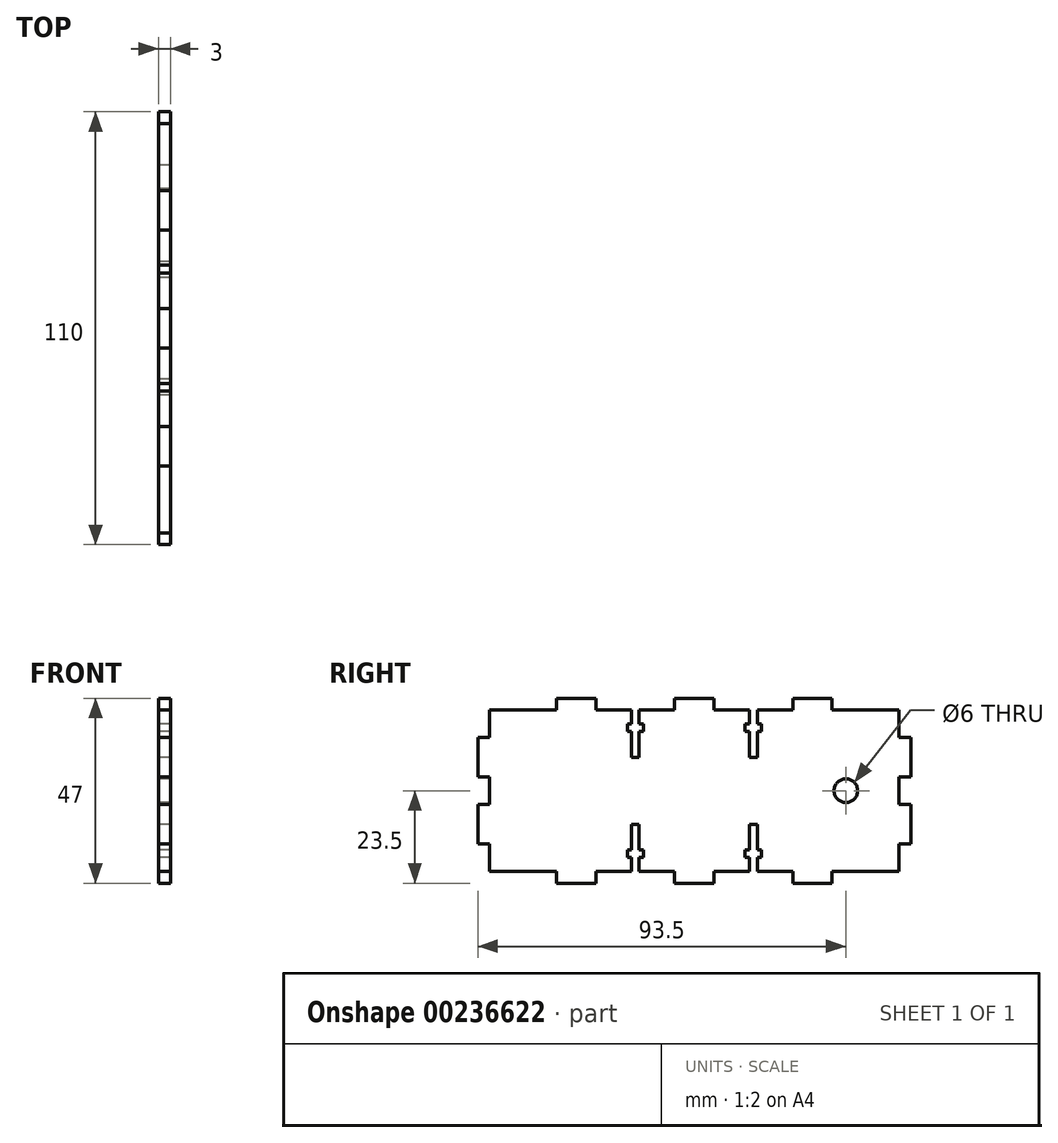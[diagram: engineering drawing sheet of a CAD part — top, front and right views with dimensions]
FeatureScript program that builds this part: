
annotation { "Feature Type Name" : "Feature", "Feature Type Description" : "" }
export const myFeature = defineFeature(function(context is Context, id is Id, definition is map)
    precondition{}
    {
        {
            var Q0;
            Q0=qCreatedBy(makeId("Right.planeOp"),FACE);
            var sketch = newSketch(context, id + "F0", { "sketchPlane" : qUnion([Q0])});
            skLineSegment(sketch, "E0", {"start": v(0, 0) * mm, "end": v(0, 7) * mm});
            skLineSegment(sketch, "E1", {"start": v(0, 7) * mm, "end": v(-3, 7) * mm});
            skLineSegment(sketch, "E2", {"start": v(-3, 7) * mm, "end": v(-3, 17) * mm});
            skLineSegment(sketch, "E3", {"start": v(-3, 17) * mm, "end": v(0, 17) * mm});
            skLineSegment(sketch, "E4", {"start": v(0, 17) * mm, "end": v(0, 20.5) * mm});
            skLineSegment(sketch, "E5", {"start": v(0, 0) * mm, "end": v(17, 0) * mm});
            skLineSegment(sketch, "E6", {"start": v(17, 0) * mm, "end": v(17, -3) * mm});
            skLineSegment(sketch, "E7", {"start": v(17, -3) * mm, "end": v(27, -3) * mm});
            skLineSegment(sketch, "E8", {"start": v(27, 0) * mm, "end": v(27, -3) * mm});
            skLineSegment(sketch, "E9", {"start": v(27, 0) * mm, "end": v(36, 0) * mm});
            skLineSegment(sketch, "E10", {"start": v(36, 0) * mm, "end": v(36, 3.5) * mm});
            skLineSegment(sketch, "E11", {"start": v(36, 3.5) * mm, "end": v(35, 3.5) * mm});
            skLineSegment(sketch, "E12", {"start": v(35, 3.5) * mm, "end": v(35, 5.5) * mm});
            skLineSegment(sketch, "E13", {"start": v(35, 5.5) * mm, "end": v(36, 5.5) * mm});
            skLineSegment(sketch, "E14", {"start": v(36, 5.5) * mm, "end": v(36, 12) * mm});
            skLineSegment(sketch, "E15", {"start": v(36, 12) * mm, "end": v(38, 12) * mm});
            skLineSegment(sketch, "E16", {"start": v(38, 12) * mm, "end": v(38, 5.5) * mm});
            skLineSegment(sketch, "E17", {"start": v(38, 5.5) * mm, "end": v(39.14, 5.5) * mm});
            skLineSegment(sketch, "E18", {"start": v(38, 3.5) * mm, "end": v(39.14, 3.5) * mm});
            skLineSegment(sketch, "E19", {"start": v(38, 0) * mm, "end": v(38, 3.5) * mm});
            skLineSegment(sketch, "E20", {"start": v(38, 0) * mm, "end": v(47, 0) * mm});
            skLineSegment(sketch, "E21", {"start": v(39.14, 3.5) * mm, "end": v(39.14, 5.5) * mm});
            skLineSegment(sketch, "E22", {"start": v(47, 0) * mm, "end": v(47, -3) * mm});
            skLineSegment(sketch, "E23", {"start": v(47, -3) * mm, "end": v(52, -3) * mm});
            skLineSegment(sketch, "E24", {"start": v(0, 20.5) * mm, "end": v(52, 20.5) * mm, "construction": true});
            skLineSegment(sketch, "E25", {"start": v(52, 20.5) * mm, "end": v(52, -3) * mm, "construction": true});
            skLineSegment(sketch, "E26.MirrorCS", {"start": v(35, 35.5) * mm, "end": v(36, 35.5) * mm});
            skLineSegment(sketch, "E27.MirrorCS", {"start": v(39.14, 37.5) * mm, "end": v(39.14, 35.5) * mm});
            skLineSegment(sketch, "E28.MirrorCS", {"start": v(36, 37.5) * mm, "end": v(35, 37.5) * mm});
            skLineSegment(sketch, "E29.MirrorCS", {"start": v(35, 37.5) * mm, "end": v(35, 35.5) * mm});
            skLineSegment(sketch, "E30.MirrorCS", {"start": v(38, 35.5) * mm, "end": v(39.14, 35.5) * mm});
            skLineSegment(sketch, "E31.MirrorCS", {"start": v(38, 37.5) * mm, "end": v(39.14, 37.5) * mm});
            skLineSegment(sketch, "E32.MirrorCS", {"start": v(36, 29) * mm, "end": v(38, 29) * mm});
            skLineSegment(sketch, "E33.MirrorCS", {"start": v(36, 41) * mm, "end": v(36, 37.5) * mm});
            skLineSegment(sketch, "E34.MirrorCS", {"start": v(27, 41) * mm, "end": v(27, 44) * mm});
            skLineSegment(sketch, "E35.MirrorCS", {"start": v(0, 34) * mm, "end": v(-3, 34) * mm});
            skLineSegment(sketch, "E36.MirrorCS", {"start": v(36, 35.5) * mm, "end": v(36, 29) * mm});
            skLineSegment(sketch, "E37.MirrorCS", {"start": v(38, 41) * mm, "end": v(38, 37.5) * mm});
            skLineSegment(sketch, "E38.MirrorCS", {"start": v(27, 41) * mm, "end": v(36, 41) * mm});
            skLineSegment(sketch, "E39.MirrorCS", {"start": v(38, 29) * mm, "end": v(38, 35.5) * mm});
            skLineSegment(sketch, "E40.MirrorCS", {"start": v(38, 41) * mm, "end": v(47, 41) * mm});
            skLineSegment(sketch, "E41.MirrorCS", {"start": v(0, 41) * mm, "end": v(17, 41) * mm});
            skLineSegment(sketch, "E42.MirrorCS", {"start": v(17, 41) * mm, "end": v(17, 44) * mm});
            skLineSegment(sketch, "E43.MirrorCS", {"start": v(-3, 34) * mm, "end": v(-3, 24) * mm});
            skLineSegment(sketch, "E44.MirrorCS", {"start": v(-3, 24) * mm, "end": v(0, 24) * mm});
            skLineSegment(sketch, "E45.MirrorCS", {"start": v(0, 41) * mm, "end": v(0, 34) * mm});
            skLineSegment(sketch, "E46.MirrorCS", {"start": v(47, 41) * mm, "end": v(47, 44) * mm});
            skLineSegment(sketch, "E47.MirrorCS", {"start": v(17, 44) * mm, "end": v(27, 44) * mm});
            skLineSegment(sketch, "E48.MirrorCS", {"start": v(0, 24) * mm, "end": v(0, 20.5) * mm});
            skLineSegment(sketch, "E49.MirrorCS", {"start": v(47, 44) * mm, "end": v(52, 44) * mm});
            skLineSegment(sketch, "E50.MirrorCS", {"start": v(52, 20.5) * mm, "end": v(52, 44) * mm, "construction": true});
            skLineSegment(sketch, "E51.MirrorCS", {"start": v(69, 37.5) * mm, "end": v(69, 35.5) * mm});
            skLineSegment(sketch, "E52.MirrorCS", {"start": v(69, 35.5) * mm, "end": v(68, 35.5) * mm});
            skLineSegment(sketch, "E53.MirrorCS", {"start": v(68, 29) * mm, "end": v(66, 29) * mm});
            skLineSegment(sketch, "E54.MirrorCS", {"start": v(66, 37.5) * mm, "end": v(64.86, 37.5) * mm});
            skLineSegment(sketch, "E55.MirrorCS", {"start": v(66, 3.5) * mm, "end": v(64.86, 3.5) * mm});
            skLineSegment(sketch, "E56.MirrorCS", {"start": v(68, 3.5) * mm, "end": v(69, 3.5) * mm});
            skLineSegment(sketch, "E57.MirrorCS", {"start": v(69, 3.5) * mm, "end": v(69, 5.5) * mm});
            skLineSegment(sketch, "E58.MirrorCS", {"start": v(66, 5.5) * mm, "end": v(64.86, 5.5) * mm});
            skLineSegment(sketch, "E59.MirrorCS", {"start": v(64.86, 37.5) * mm, "end": v(64.86, 35.5) * mm});
            skLineSegment(sketch, "E60.MirrorCS", {"start": v(66, 35.5) * mm, "end": v(64.86, 35.5) * mm});
            skLineSegment(sketch, "E61.MirrorCS", {"start": v(69, 5.5) * mm, "end": v(68, 5.5) * mm});
            skLineSegment(sketch, "E62.MirrorCS", {"start": v(64.86, 3.5) * mm, "end": v(64.86, 5.5) * mm});
            skLineSegment(sketch, "E63.MirrorCS", {"start": v(68, 37.5) * mm, "end": v(69, 37.5) * mm});
            skLineSegment(sketch, "E64.MirrorCS", {"start": v(68, 12) * mm, "end": v(66, 12) * mm});
            skLineSegment(sketch, "E65.MirrorCS", {"start": v(77, 41) * mm, "end": v(77, 44) * mm});
            skLineSegment(sketch, "E66.MirrorCS", {"start": v(66, 0) * mm, "end": v(57, 0) * mm});
            skLineSegment(sketch, "E67.MirrorCS", {"start": v(104, 41) * mm, "end": v(104, 34) * mm});
            skLineSegment(sketch, "E68.MirrorCS", {"start": v(87, 41) * mm, "end": v(87, 44) * mm});
            skLineSegment(sketch, "E69.MirrorCS", {"start": v(66, 0) * mm, "end": v(66, 3.5) * mm});
            skLineSegment(sketch, "E70.MirrorCS", {"start": v(66, 12) * mm, "end": v(66, 5.5) * mm});
            skLineSegment(sketch, "E71.MirrorCS", {"start": v(68, 35.5) * mm, "end": v(68, 29) * mm});
            skLineSegment(sketch, "E72.MirrorCS", {"start": v(104, 24) * mm, "end": v(104, 20.5) * mm});
            skLineSegment(sketch, "E73.MirrorCS", {"start": v(104, 34) * mm, "end": v(107, 34) * mm});
            skLineSegment(sketch, "E74.MirrorCS", {"start": v(87, 44) * mm, "end": v(77, 44) * mm});
            skLineSegment(sketch, "E75.MirrorCS", {"start": v(68, 0) * mm, "end": v(68, 3.5) * mm});
            skLineSegment(sketch, "E76.MirrorCS", {"start": v(68, 41) * mm, "end": v(68, 37.5) * mm});
            skLineSegment(sketch, "E77.MirrorCS", {"start": v(87, 0) * mm, "end": v(87, -3) * mm});
            skLineSegment(sketch, "E78.MirrorCS", {"start": v(104, 0) * mm, "end": v(104, 7) * mm});
            skLineSegment(sketch, "E79.MirrorCS", {"start": v(57, 44) * mm, "end": v(52, 44) * mm});
            skLineSegment(sketch, "E80.MirrorCS", {"start": v(77, 0) * mm, "end": v(68, 0) * mm});
            skLineSegment(sketch, "E81.MirrorCS", {"start": v(57, 0) * mm, "end": v(57, -3) * mm});
            skLineSegment(sketch, "E82.MirrorCS", {"start": v(104, 7) * mm, "end": v(107, 7) * mm});
            skLineSegment(sketch, "E83.MirrorCS", {"start": v(77, 41) * mm, "end": v(68, 41) * mm});
            skLineSegment(sketch, "E84.MirrorCS", {"start": v(107, 34) * mm, "end": v(107, 24) * mm});
            skLineSegment(sketch, "E85.MirrorCS", {"start": v(107, 7) * mm, "end": v(107, 17) * mm});
            skLineSegment(sketch, "E86.MirrorCS", {"start": v(66, 29) * mm, "end": v(66, 35.5) * mm});
            skLineSegment(sketch, "E87.MirrorCS", {"start": v(57, -3) * mm, "end": v(52, -3) * mm});
            skLineSegment(sketch, "E88.MirrorCS", {"start": v(66, 41) * mm, "end": v(66, 37.5) * mm});
            skLineSegment(sketch, "E89.MirrorCS", {"start": v(57, 41) * mm, "end": v(57, 44) * mm});
            skLineSegment(sketch, "E90.MirrorCS", {"start": v(66, 41) * mm, "end": v(57, 41) * mm});
            skLineSegment(sketch, "E91.MirrorCS", {"start": v(104, 20.5) * mm, "end": v(52, 20.5) * mm, "construction": true});
            skLineSegment(sketch, "E92.MirrorCS", {"start": v(107, 24) * mm, "end": v(104, 24) * mm});
            skLineSegment(sketch, "E93.MirrorCS", {"start": v(104, 0) * mm, "end": v(87, 0) * mm});
            skLineSegment(sketch, "E94.MirrorCS", {"start": v(87, -3) * mm, "end": v(77, -3) * mm});
            skLineSegment(sketch, "E95.MirrorCS", {"start": v(68, 5.5) * mm, "end": v(68, 12) * mm});
            skLineSegment(sketch, "E96.MirrorCS", {"start": v(77, 0) * mm, "end": v(77, -3) * mm});
            skLineSegment(sketch, "E97.MirrorCS", {"start": v(104, 41) * mm, "end": v(87, 41) * mm});
            skLineSegment(sketch, "E98.MirrorCS", {"start": v(104, 17) * mm, "end": v(104, 20.5) * mm});
            skLineSegment(sketch, "E99.MirrorCS", {"start": v(107, 17) * mm, "end": v(104, 17) * mm});
            skCircle(sketch, "E100", {"center": v(90.5, 20.5) * mm, "radius": 3 * mm});
            skSolve(sketch);
        }
        {
            var Q0;
            Q0=qSketchRegion(id+"F0",true);
            extrude(context, id + "F1", {"entities" : qUnion([Q0]), "depth" : 3 * mm});
        }
    });
